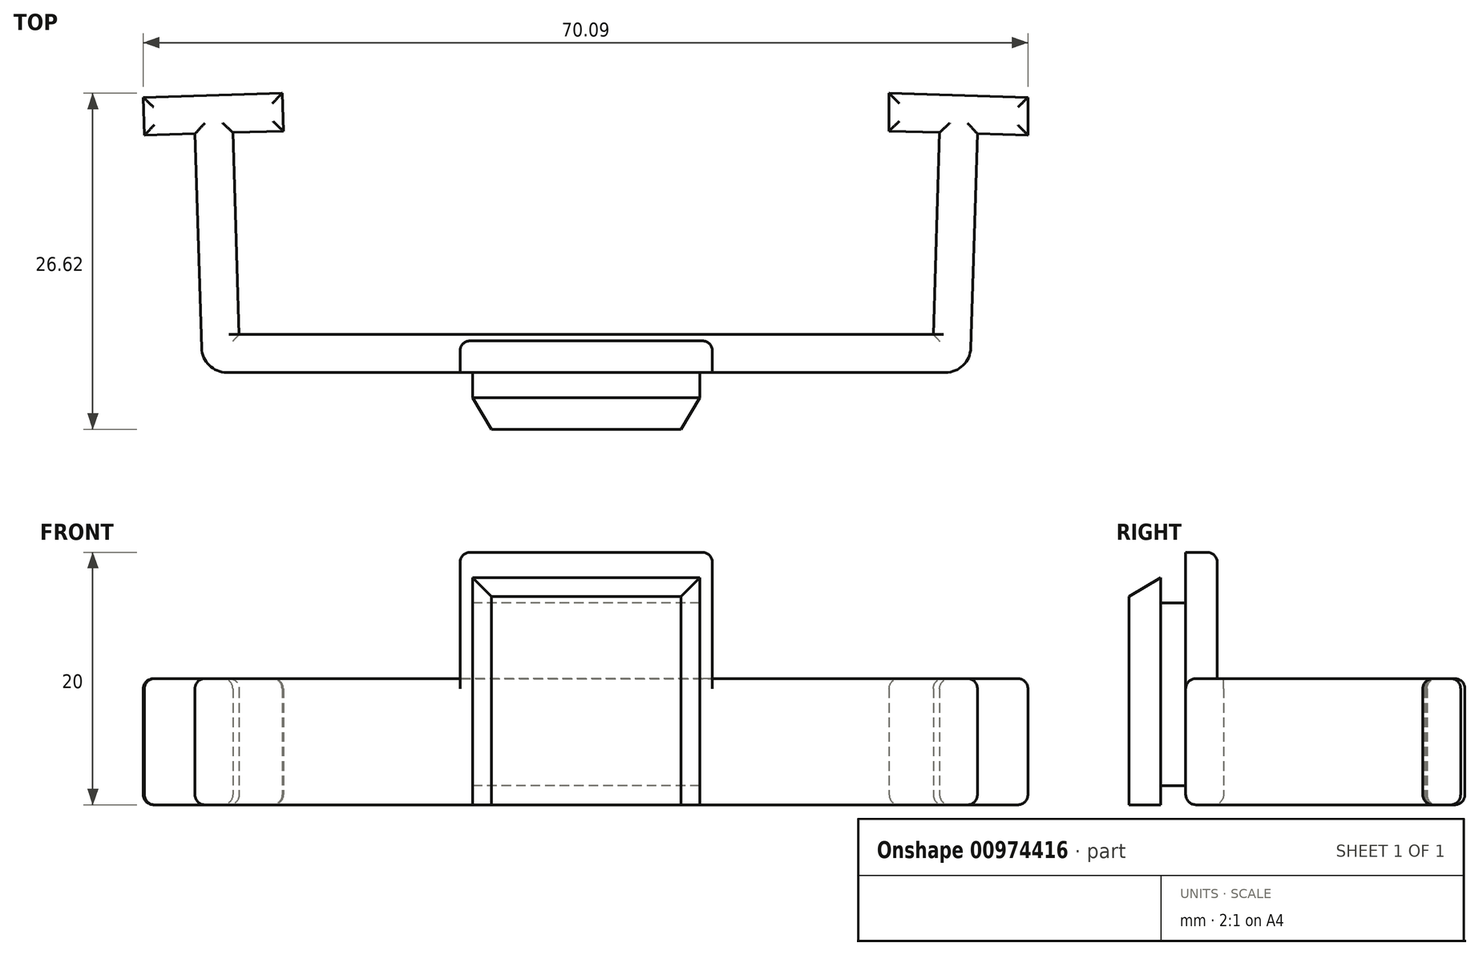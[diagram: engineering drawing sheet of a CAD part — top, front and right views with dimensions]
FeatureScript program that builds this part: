
annotation { "Feature Type Name" : "Feature", "Feature Type Description" : "" }
export const myFeature = defineFeature(function(context is Context, id is Id, definition is map)
    precondition{}
    {
        {
            var Q0;
            Q0=qCreatedBy(makeId("Top.planeOp"),FACE);
            var sketch = newSketch(context, id + "F0", { "sketchPlane" : qUnion([Q0])});
            skLineSegment(sketch, "E0", {"start": v(-27.5, 0) * mm, "end": v(27.5, 0) * mm});
            skLineSegment(sketch, "E1", {"start": v(27.5, 0) * mm, "end": v(28, 16) * mm});
            skLineSegment(sketch, "E2", {"start": v(-27.5, 0) * mm, "end": v(-28, 16) * mm});
            skPoint(sketch, "E3", {"position": v(0, 0) * mm});
            skLineSegment(sketch, "E4", {"start": v(-28, 16) * mm, "end": v(0, 0) * mm, "construction": true});
            skLineSegment(sketch, "E5", {"start": v(0, 0) * mm, "end": v(28, 16) * mm, "construction": true});
            skLineSegment(sketch, "E6", {"start": v(28, 16) * mm, "end": v(35, 15.78) * mm});
            skLineSegment(sketch, "E7", {"start": v(28, 16) * mm, "end": v(24, 16.12) * mm});
            skLineSegment(sketch, "E8.0", {"start": v(30.4, -3) * mm, "end": v(31, 15.9) * mm});
            skLineSegment(sketch, "E8.1", {"start": v(-30.4, -3) * mm, "end": v(30.4, -3) * mm});
            skLineSegment(sketch, "E8.2", {"start": v(-30.4, -3) * mm, "end": v(-31, 15.9) * mm});
            skLineSegment(sketch, "E9", {"start": v(-28, 16) * mm, "end": v(-35, 15.78) * mm});
            skLineSegment(sketch, "E10", {"start": v(-28, 16) * mm, "end": v(-24, 16.12) * mm});
            skLineSegment(sketch, "E11", {"start": v(-35, 15.78) * mm, "end": v(-35.1, 18.78) * mm});
            skLineSegment(sketch, "E12", {"start": v(-35.1, 18.78) * mm, "end": v(-24.1, 19.12) * mm});
            skLineSegment(sketch, "E13", {"start": v(-24.1, 19.12) * mm, "end": v(-24, 16.12) * mm});
            skLineSegment(sketch, "E14", {"start": v(24, 16.12) * mm, "end": v(24, 19.12) * mm});
            skLineSegment(sketch, "E15", {"start": v(24, 19.12) * mm, "end": v(35, 18.78) * mm});
            skLineSegment(sketch, "E16", {"start": v(35, 18.78) * mm, "end": v(35, 15.78) * mm});
            skSolve(sketch);
        }
        {
            var Q0;
            Q0 = qSketchRegion(id + "F0", true);
            extrude(context, id + "F1", {"entities" : qUnion([Q0]), "depth" : 10 * mm, "offsetDistance" : 25 * mm});
        }
        {
            var Q0;
            Q0=qCreatedBy(makeId("Right.planeOp"),FACE);
            var sketch = newSketch(context, id + "F2", { "sketchPlane" : qUnion([Q0])});
            skLineSegment(sketch, "E17.0", {"start": v(-3, 10) * mm, "end": v(-3, 0) * mm});
            skLineSegment(sketch, "E18.0", {"start": v(-3, 10) * mm, "end": v(15.9, 10) * mm});
            skLineSegment(sketch, "E19", {"start": v(-3, 10) * mm, "end": v(-3, 20) * mm});
            skLineSegment(sketch, "E20", {"start": v(-3, 20) * mm, "end": v(-0.5, 20) * mm});
            skLineSegment(sketch, "E21", {"start": v(-0.5, 20) * mm, "end": v(-0.5, 10) * mm});
            skLineSegment(sketch, "E22", {"start": v(-3, 16) * mm, "end": v(-5, 16) * mm});
            skLineSegment(sketch, "E23", {"start": v(-5, 16) * mm, "end": v(-5, 1.5) * mm});
            skLineSegment(sketch, "E24", {"start": v(-5, 1.5) * mm, "end": v(-3, 1.5) * mm});
            skLineSegment(sketch, "E25", {"start": v(-5, 0) * mm, "end": v(-5, 18) * mm});
            skLineSegment(sketch, "E26", {"start": v(-5, 18) * mm, "end": v(-7.5, 18) * mm});
            skLineSegment(sketch, "E27", {"start": v(-7.5, 18) * mm, "end": v(-7.5, 0) * mm});
            skLineSegment(sketch, "E28", {"start": v(-7.5, 0) * mm, "end": v(-5, 0) * mm});
            skSolve(sketch);
        }
        {
            var Q0;
            {var subQ0=sQuery(id+"F2.wireOp",EDGE,"E20");Q0=makeQuery(id+"F2.imprint","IMPRINT",FACE,{"disambiguationData":[TD([[makeQuery(id+"F2.imprint","IMPRINT",EDGE,{"derivedFrom":subQ0}),-1.0]])]});}
            extrude(context, id + "F3", {"entities" : qUnion([Q0]), "operationType" : NewBodyOperationType.ADD, "endBound" : BoundingType.SYMMETRIC, "depth" : 20 * mm, "offsetDistance" : 25 * mm});
        }
        {
            var Q0;
            {var subQ0=sQuery(id+"F2.wireOp",EDGE,"E22");Q0=makeQuery(id+"F2.imprint","IMPRINT",FACE,{"disambiguationData":[TD([[makeQuery(id+"F2.imprint","IMPRINT",EDGE,{"derivedFrom":subQ0}),1.0]])]});}
            extrude(context, id + "F4", {"entities" : qUnion([Q0]), "operationType" : NewBodyOperationType.ADD, "endBound" : BoundingType.SYMMETRIC, "depth" : 18 * mm, "offsetDistance" : 25 * mm});
        }
        {
            var Q0;
            {var subQ0=sQuery(id+"F2.wireOp",EDGE,"E26");Q0=makeQuery(id+"F2.imprint","IMPRINT",FACE,{"disambiguationData":[TD([[makeQuery(id+"F2.imprint","IMPRINT",EDGE,{"derivedFrom":subQ0}),1.0]])]});}
            extrude(context, id + "F5", {"entities" : qUnion([Q0]), "operationType" : NewBodyOperationType.ADD, "endBound" : BoundingType.SYMMETRIC, "depth" : 18 * mm, "offsetDistance" : 25 * mm});
        }
        {
            var Q0;
            Q0=makeQuery(id+"F5.opExtrude","SWEPT_EDGE",EDGE,{"disambiguationData":[OSD([sQuery(id+"F2.wireOp",EDGE,"E26"),sQuery(id+"F2.wireOp",EDGE,"E27")])]});
            var Q1;
            Q1=makeQuery(id+"F5.opExtrude","CAP_EDGE",EDGE,{"disambiguationData":[OSD([sQuery(id+"F2.wireOp",EDGE,"E27")])],"isStart":true});
            var Q2;
            Q2=makeQuery(id+"F5.opExtrude","CAP_EDGE",EDGE,{"disambiguationData":[OSD([sQuery(id+"F2.wireOp",EDGE,"E27")])],"isStart":false});
            chamfer(context, id + "F6", {"entities" : qUnion([Q0, Q1, Q2]), "chamferType" : ChamferType.TWO_OFFSETS, "width1" : 1.5 * mm, "oppositeDirection" : false, "width2" : 2.5 * mm, "tangentPropagation" : true});
        }
        {
            var Q0;
            Q0=makeQuery(id+"F1.opExtrude","CAP_FACE",FACE,{"disambiguationData":[OSD([sQuery(id+"F0.wireOp",EDGE,"E0"),sQuery(id+"F0.wireOp",EDGE,"E1"),sQuery(id+"F0.wireOp",EDGE,"E2"),sQuery(id+"F0.wireOp",EDGE,"E6"),sQuery(id+"F0.wireOp",EDGE,"E7"),sQuery(id+"F0.wireOp",EDGE,"E8.0"),sQuery(id+"F0.wireOp",EDGE,"E8.1"),sQuery(id+"F0.wireOp",EDGE,"E8.2"),sQuery(id+"F0.wireOp",EDGE,"E9"),sQuery(id+"F0.wireOp",EDGE,"E10"),sQuery(id+"F0.wireOp",EDGE,"E11"),sQuery(id+"F0.wireOp",EDGE,"E12"),sQuery(id+"F0.wireOp",EDGE,"E13"),sQuery(id+"F0.wireOp",EDGE,"E14"),sQuery(id+"F0.wireOp",EDGE,"E15"),sQuery(id+"F0.wireOp",EDGE,"E16")])],"isStart":true});
            fillet(context, id + "F7", {"entities" : qUnion([Q0]), "radius" : 0.8 * mm, "tangentPropagation" : true, "allowEdgeOverflow" : false});
        }
        {
            var Q0;
            Q0=makeQuery(id+"F1.opExtrude","CAP_EDGE",EDGE,{"disambiguationData":[OSD([sQuery(id+"F0.wireOp",EDGE,"E12")])],"isStart":false});
            var Q1;
            Q1=makeQuery(id+"F1.opExtrude","CAP_EDGE",EDGE,{"disambiguationData":[OSD([sQuery(id+"F0.wireOp",EDGE,"E11")])],"isStart":false});
            var Q2;
            Q2=makeQuery(id+"F1.opExtrude","CAP_EDGE",EDGE,{"disambiguationData":[OSD([sQuery(id+"F0.wireOp",EDGE,"E9")])],"isStart":false});
            var Q3;
            Q3=makeQuery(id+"F1.opExtrude","CAP_EDGE",EDGE,{"disambiguationData":[OSD([sQuery(id+"F0.wireOp",EDGE,"E10")])],"isStart":false});
            var Q4;
            Q4=makeQuery(id+"F1.opExtrude","CAP_EDGE",EDGE,{"disambiguationData":[OSD([sQuery(id+"F0.wireOp",EDGE,"E13")])],"isStart":false});
            var Q5;
            Q5=makeQuery(id+"F1.opExtrude","CAP_EDGE",EDGE,{"disambiguationData":[OSD([sQuery(id+"F0.wireOp",EDGE,"E2")])],"isStart":false});
            var Q6;
            Q6=makeQuery(id+"F1.opExtrude","CAP_EDGE",EDGE,{"disambiguationData":[OSD([sQuery(id+"F0.wireOp",EDGE,"E8.2")])],"isStart":false});
            var Q7;
            {var subQ1=sQuery(id+"F0.wireOp",EDGE,"E8.2");var subQ2=sQuery(id+"F0.wireOp",EDGE,"E8.1");Q7=makeQuery(id+"F3.boolean.opBoolean","SPLIT",EDGE,{"disambiguationData":[TD([makeQuery(id+"F1.opExtrude","SWEPT_FACE",FACE,{"disambiguationData":[OSD([subQ1])]})])],"derivedFrom":makeQuery(id+"F1.opExtrude","CAP_EDGE",EDGE,{"disambiguationData":[OSD([subQ2])],"isStart":false})});}
            var Q8;
            {var subQ1=sQuery(id+"F0.wireOp",EDGE,"E8.1");var subQ2=sQuery(id+"F0.wireOp",EDGE,"E8.0");Q8=makeQuery(id+"F3.boolean.opBoolean","SPLIT",EDGE,{"disambiguationData":[TD([makeQuery(id+"F1.opExtrude","SWEPT_FACE",FACE,{"disambiguationData":[OSD([subQ2])]})])],"derivedFrom":makeQuery(id+"F1.opExtrude","CAP_EDGE",EDGE,{"disambiguationData":[OSD([subQ1])],"isStart":false})});}
            var Q9;
            Q9=makeQuery(id+"F1.opExtrude","CAP_EDGE",EDGE,{"disambiguationData":[OSD([sQuery(id+"F0.wireOp",EDGE,"E8.0")])],"isStart":false});
            var Q10;
            Q10=makeQuery(id+"F1.opExtrude","CAP_EDGE",EDGE,{"disambiguationData":[OSD([sQuery(id+"F0.wireOp",EDGE,"E6")])],"isStart":false});
            var Q11;
            Q11=makeQuery(id+"F1.opExtrude","CAP_EDGE",EDGE,{"disambiguationData":[OSD([sQuery(id+"F0.wireOp",EDGE,"E16")])],"isStart":false});
            var Q12;
            Q12=makeQuery(id+"F1.opExtrude","CAP_EDGE",EDGE,{"disambiguationData":[OSD([sQuery(id+"F0.wireOp",EDGE,"E15")])],"isStart":false});
            var Q13;
            Q13=makeQuery(id+"F1.opExtrude","CAP_EDGE",EDGE,{"disambiguationData":[OSD([sQuery(id+"F0.wireOp",EDGE,"E14")])],"isStart":false});
            var Q14;
            Q14=makeQuery(id+"F1.opExtrude","CAP_EDGE",EDGE,{"disambiguationData":[OSD([sQuery(id+"F0.wireOp",EDGE,"E7")])],"isStart":false});
            var Q15;
            Q15=makeQuery(id+"F1.opExtrude","CAP_EDGE",EDGE,{"disambiguationData":[OSD([sQuery(id+"F0.wireOp",EDGE,"E1")])],"isStart":false});
            fillet(context, id + "F8", {"entities" : qUnion([Q0, Q1, Q2, Q3, Q4, Q5, Q6, Q7, Q8, Q9, Q10, Q11, Q12, Q13, Q14, Q15]), "radius" : 0.8 * mm, "tangentPropagation" : true, "allowEdgeOverflow" : false});
        }
        {
            var Q0;
            Q0=makeQuery(id+"F3.opExtrude","SWEPT_EDGE",EDGE,{"disambiguationData":[OSD([sQuery(id+"F2.wireOp",EDGE,"E20"),sQuery(id+"F2.wireOp",EDGE,"E21")])]});
            var Q1;
            Q1=makeQuery(id+"F3.opExtrude","CAP_EDGE",EDGE,{"disambiguationData":[OSD([sQuery(id+"F2.wireOp",EDGE,"E21")])],"isStart":true});
            var Q2;
            Q2=makeQuery(id+"F3.opExtrude","CAP_EDGE",EDGE,{"disambiguationData":[OSD([sQuery(id+"F2.wireOp",EDGE,"E21")])],"isStart":false});
            var Q3;
            Q3=makeQuery(id+"F3.opExtrude","CAP_EDGE",EDGE,{"disambiguationData":[OSD([sQuery(id+"F2.wireOp",EDGE,"E20")])],"isStart":false});
            var Q4;
            Q4=makeQuery(id+"F3.opExtrude","CAP_EDGE",EDGE,{"disambiguationData":[OSD([sQuery(id+"F2.wireOp",EDGE,"E20")])],"isStart":true});
            fillet(context, id + "F9", {"entities" : qUnion([Q0, Q1, Q2, Q3, Q4]), "radius" : 0.8 * mm, "tangentPropagation" : true, "allowEdgeOverflow" : false});
        }
        {
            var Q0;
            Q0=makeQuery(id+"F1.opExtrude","SWEPT_EDGE",EDGE,{"disambiguationData":[OSD([sQuery(id+"F0.wireOp",EDGE,"E8.1"),sQuery(id+"F0.wireOp",EDGE,"E8.2")])]});
            var Q1;
            Q1=makeQuery(id+"F1.opExtrude","SWEPT_EDGE",EDGE,{"disambiguationData":[OSD([sQuery(id+"F0.wireOp",EDGE,"E8.0"),sQuery(id+"F0.wireOp",EDGE,"E8.1")])]});
            fillet(context, id + "F10", {"entities" : qUnion([Q0, Q1]), "radius" : 2 * mm, "tangentPropagation" : true, "allowEdgeOverflow" : false});
        }
    });
